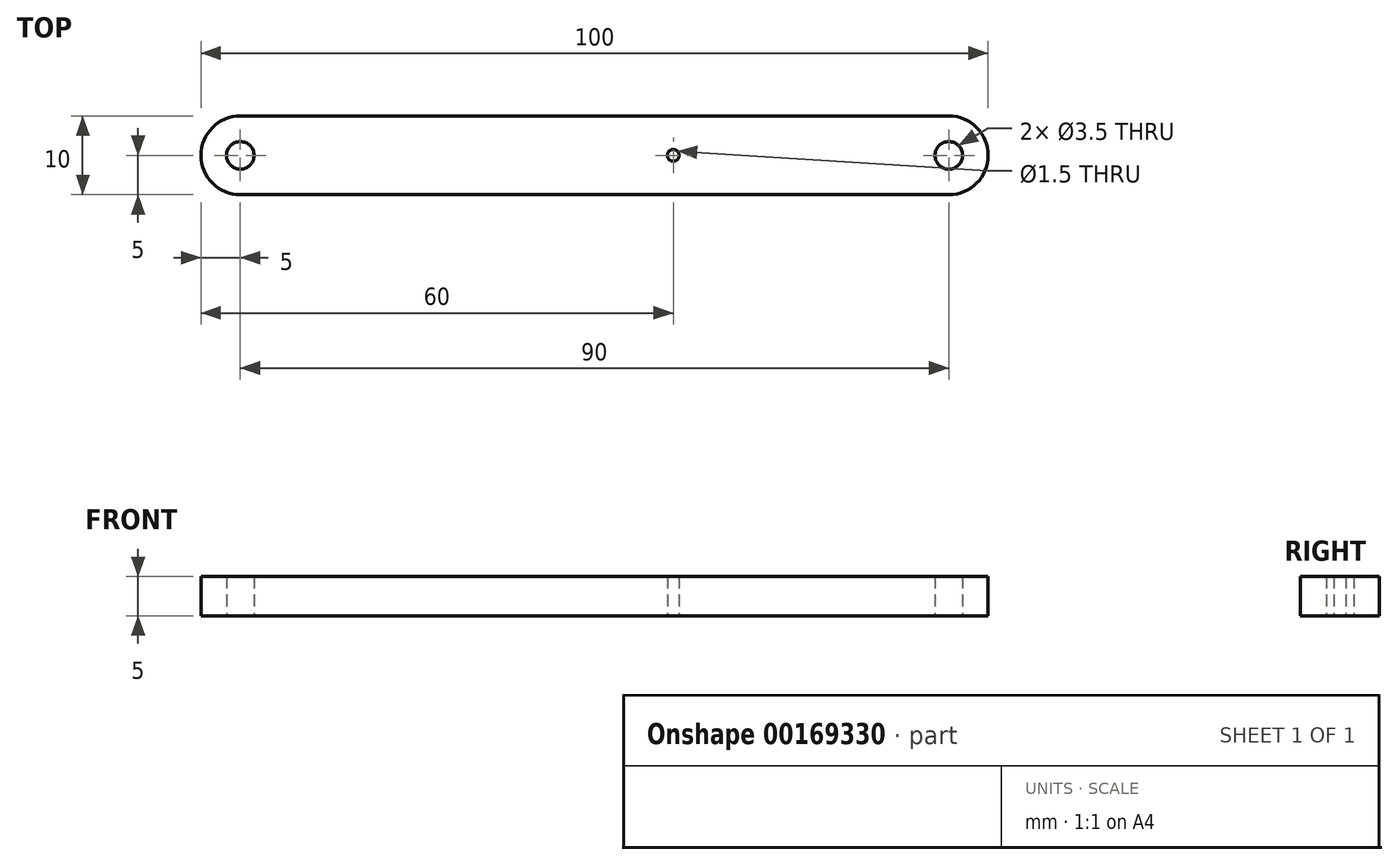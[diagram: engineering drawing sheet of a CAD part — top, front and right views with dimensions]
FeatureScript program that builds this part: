
annotation { "Feature Type Name" : "Feature", "Feature Type Description" : "" }
export const myFeature = defineFeature(function(context is Context, id is Id, definition is map)
    precondition{}
    {
        {
            var Q0;
            Q0=qCreatedBy(makeId("Top.planeOp"),FACE);
            var sketch = newSketch(context, id + "F0", { "sketchPlane" : qUnion([Q0])});
            skLineSegment(sketch, "E0.bottom", {"start": v(45, 5) * mm, "end": v(-45, 5) * mm});
            skLineSegment(sketch, "E0.top", {"start": v(45, -5) * mm, "end": v(-45, -5) * mm});
            skLineSegment(sketch, "E0.left", {"start": v(50, 0) * mm, "end": v(50, 0) * mm});
            skLineSegment(sketch, "E0.right", {"start": v(-50, 0) * mm, "end": v(-50, 0) * mm});
            skPoint(sketch, "E0.middle", {"position": v(0, 0) * mm});
            skPoint(sketch, "E1.visualSharp", {"position": v(-50, 5) * mm});
            skArc(sketch, "E1.filletArc", {"start": v(-45, 5) * mm, "mid": v(-48.54, 3.54) * mm, "end": v(-50, 0) * mm});
            skPoint(sketch, "E2.visualSharp", {"position": v(-50, -5) * mm});
            skArc(sketch, "E2.filletArc", {"start": v(-50, 0) * mm, "mid": v(-48.54, -3.54) * mm, "end": v(-45, -5) * mm});
            skPoint(sketch, "E3.visualSharp", {"position": v(50, -5) * mm});
            skArc(sketch, "E3.filletArc", {"start": v(45, -5) * mm, "mid": v(48.54, -3.54) * mm, "end": v(50, 0) * mm});
            skPoint(sketch, "E4.visualSharp", {"position": v(50, 5) * mm});
            skArc(sketch, "E4.filletArc", {"start": v(50, 0) * mm, "mid": v(48.54, 3.54) * mm, "end": v(45, 5) * mm});
            skCircle(sketch, "E5", {"center": v(-45, 0) * mm, "radius": 1.75 * mm});
            skCircle(sketch, "E6", {"center": v(45, 0) * mm, "radius": 1.75 * mm});
            skCircle(sketch, "E7", {"center": v(10, 0) * mm, "radius": 0.75 * mm});
            skSolve(sketch);
        }
        {
            var Q0;
            Q0=makeQuery(id+"F0.imprint","IMPRINT",FACE,{"disambiguationData":[TD([[makeQuery(id+"F0.imprint","IMPRINT",EDGE,{"derivedFrom":sQuery(id+"F0.wireOp",EDGE,"E0.bottom")}),1.0]])]});
            extrude(context, id + "F1", {"entities" : qUnion([Q0]), "depth" : 5 * mm});
        }
    });
